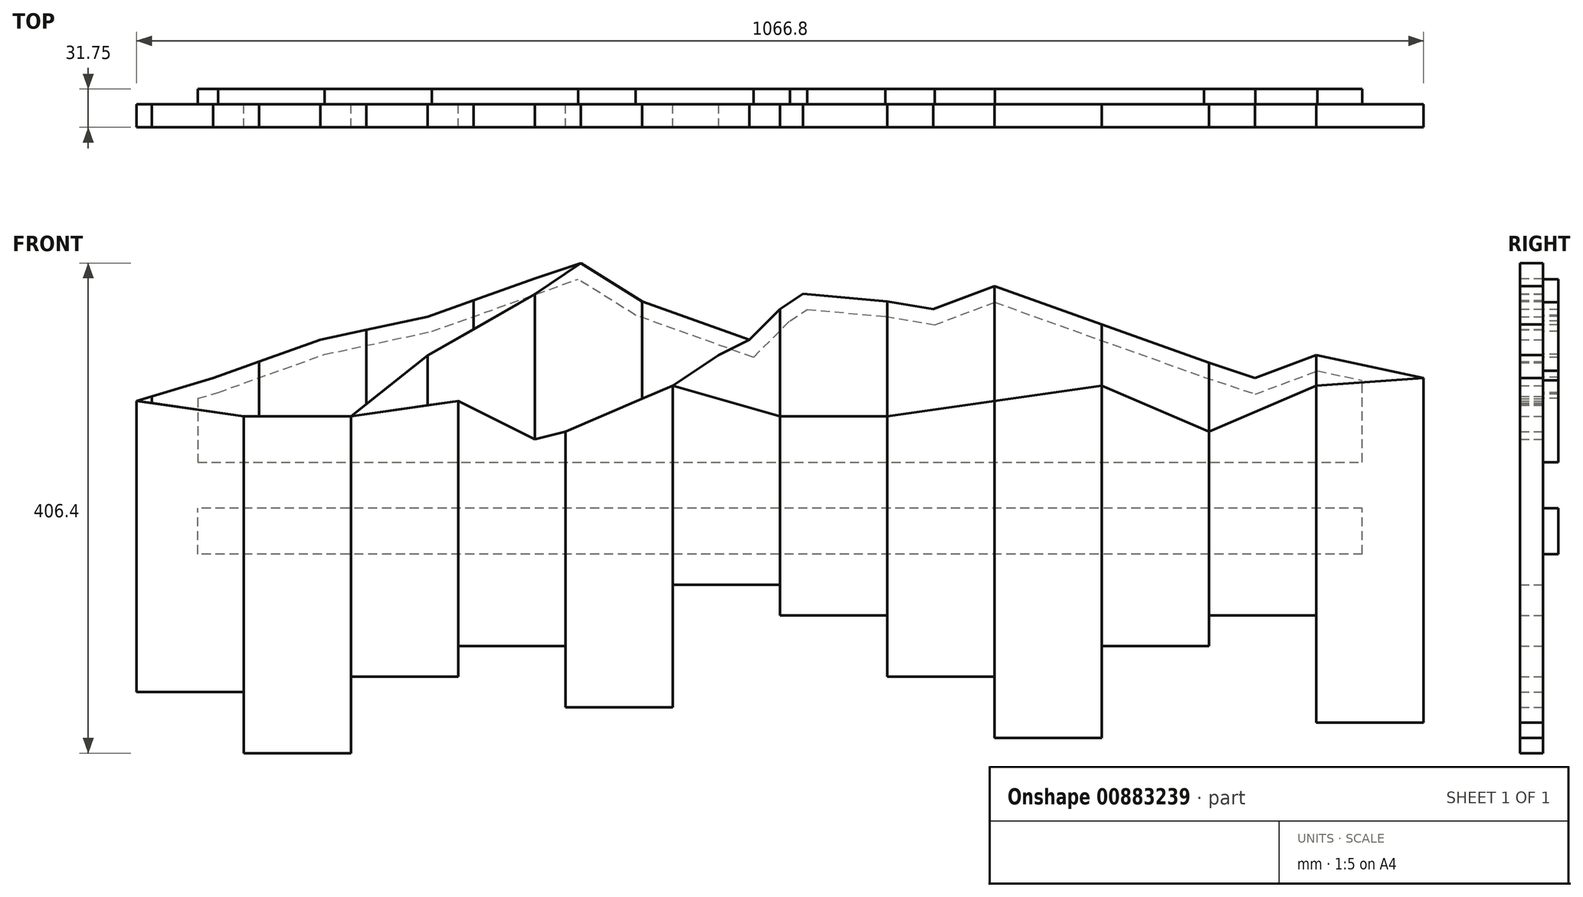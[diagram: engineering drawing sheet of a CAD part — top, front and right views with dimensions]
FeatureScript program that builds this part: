
annotation { "Feature Type Name" : "Feature", "Feature Type Description" : "" }
export const myFeature = defineFeature(function(context is Context, id is Id, definition is map)
    precondition{}
    {
        {
            var Q0;
            Q0=qCreatedBy(makeId("Front.planeOp"),FACE);
            var sketch = newSketch(context, id + "F0", { "sketchPlane" : qUnion([Q0])});
            skLineSegment(sketch, "E0.right", {"start": v(355.6, 304.8) * mm, "end": v(355.6, 76.2) * mm});
            skLineSegment(sketch, "E1.top", {"start": v(355.6, 76.2) * mm, "end": v(444.5, 76.2) * mm});
            skLineSegment(sketch, "E1.right", {"start": v(444.5, 342.9) * mm, "end": v(444.5, 76.2) * mm});
            skLineSegment(sketch, "E2.top", {"start": v(444.5, 177.8) * mm, "end": v(533.4, 177.8) * mm});
            skLineSegment(sketch, "E2.left", {"start": v(444.5, 342.9) * mm, "end": v(444.5, 177.8) * mm});
            skLineSegment(sketch, "E2.right", {"start": v(533.4, 406.4) * mm, "end": v(533.4, 177.8) * mm});
            skLineSegment(sketch, "E3.top", {"start": v(533.4, 152.4) * mm, "end": v(622.3, 152.4) * mm});
            skLineSegment(sketch, "E3.left", {"start": v(533.4, 406.4) * mm, "end": v(533.4, 152.4) * mm});
            skLineSegment(sketch, "E3.right", {"start": v(622.3, 412.75) * mm, "end": v(622.3, 152.4) * mm});
            skLineSegment(sketch, "E4.top", {"start": v(622.3, 101.6) * mm, "end": v(711.2, 101.6) * mm});
            skLineSegment(sketch, "E4.left", {"start": v(622.3, 412.75) * mm, "end": v(622.3, 101.6) * mm});
            skLineSegment(sketch, "E4.right", {"start": v(711.2, 425.45) * mm, "end": v(711.2, 101.6) * mm});
            skLineSegment(sketch, "E5.bottom", {"start": v(711.2, 425.45) * mm, "end": v(800.1, 393.7) * mm});
            skLineSegment(sketch, "E5.top", {"start": v(711.2, 50.8) * mm, "end": v(800.1, 50.8) * mm});
            skLineSegment(sketch, "E5.left", {"start": v(711.2, 425.45) * mm, "end": v(711.2, 50.8) * mm});
            skLineSegment(sketch, "E5.right", {"start": v(800.1, 393.7) * mm, "end": v(800.1, 50.8) * mm});
            skLineSegment(sketch, "E6.bottom", {"start": v(800.1, 393.7) * mm, "end": v(889, 361.95) * mm});
            skLineSegment(sketch, "E6.top", {"start": v(800.1, 127) * mm, "end": v(889, 127) * mm});
            skLineSegment(sketch, "E6.left", {"start": v(800.1, 393.7) * mm, "end": v(800.1, 127) * mm});
            skLineSegment(sketch, "E6.right", {"start": v(889, 361.95) * mm, "end": v(889, 127) * mm});
            skLineSegment(sketch, "E7.top", {"start": v(889, 152.4) * mm, "end": v(977.9, 152.4) * mm});
            skLineSegment(sketch, "E7.left", {"start": v(889, 361.95) * mm, "end": v(889, 152.4) * mm});
            skLineSegment(sketch, "E7.right", {"start": v(977.9, 368.3) * mm, "end": v(977.9, 152.4) * mm});
            skLineSegment(sketch, "E8.bottom", {"start": v(977.9, 368.3) * mm, "end": v(1066.8, 349.25) * mm});
            skLineSegment(sketch, "E8.top", {"start": v(977.9, 63.5) * mm, "end": v(1066.8, 63.5) * mm});
            skLineSegment(sketch, "E8.left", {"start": v(977.9, 368.3) * mm, "end": v(977.9, 63.5) * mm});
            skLineSegment(sketch, "E8.right", {"start": v(1066.8, 349.25) * mm, "end": v(1066.8, 63.5) * mm});
            skLineSegment(sketch, "E9", {"start": v(482.6, 368.3) * mm, "end": v(508, 381) * mm});
            skLineSegment(sketch, "E10", {"start": v(508, 381) * mm, "end": v(533.4, 406.4) * mm});
            skLineSegment(sketch, "E11", {"start": v(533.4, 406.4) * mm, "end": v(552.45, 419.1) * mm});
            skLineSegment(sketch, "E12", {"start": v(552.45, 419.1) * mm, "end": v(622.3, 412.75) * mm});
            skLineSegment(sketch, "E13", {"start": v(622.3, 412.75) * mm, "end": v(660.4, 406.4) * mm});
            skLineSegment(sketch, "E14", {"start": v(660.4, 406.4) * mm, "end": v(711.2, 425.45) * mm});
            skLineSegment(sketch, "E15", {"start": v(889, 361.95) * mm, "end": v(927.1, 349.25) * mm});
            skLineSegment(sketch, "E16", {"start": v(927.1, 349.25) * mm, "end": v(977.9, 368.3) * mm});
            skLineSegment(sketch, "E17", {"start": v(444.5, 342.9) * mm, "end": v(355.6, 304.8) * mm});
            skLineSegment(sketch, "E18", {"start": v(444.5, 342.9) * mm, "end": v(482.6, 368.3) * mm});
            skLineSegment(sketch, "E19", {"start": v(419.1, 412.75) * mm, "end": v(419.1, 332.01) * mm});
            skLineSegment(sketch, "E20", {"start": v(508, 381) * mm, "end": v(419.1, 412.75) * mm});
            skLineSegment(sketch, "E21", {"start": v(419.1, 412.75) * mm, "end": v(368.3, 444.5) * mm});
            skLineSegment(sketch, "E22", {"start": v(368.3, 444.5) * mm, "end": v(330.2, 431.8) * mm});
            skLineSegment(sketch, "E23", {"start": v(330.2, 418.65) * mm, "end": v(330.2, 298.45) * mm});
            skLineSegment(sketch, "E24", {"start": v(355.6, 127) * mm, "end": v(266.7, 127) * mm});
            skLineSegment(sketch, "E25", {"start": v(241.3, 400.05) * mm, "end": v(330.2, 431.8) * mm});
            skLineSegment(sketch, "E26", {"start": v(266.7, 127) * mm, "end": v(266.7, 101.6) * mm});
            skLineSegment(sketch, "E27", {"start": v(266.7, 101.6) * mm, "end": v(177.8, 101.6) * mm});
            skLineSegment(sketch, "E28", {"start": v(152.4, 381) * mm, "end": v(241.3, 400.05) * mm});
            skLineSegment(sketch, "E29", {"start": v(177.8, 101.6) * mm, "end": v(177.8, 38.1) * mm});
            skLineSegment(sketch, "E30", {"start": v(177.8, 38.1) * mm, "end": v(88.9, 38.1) * mm});
            skLineSegment(sketch, "E31", {"start": v(88.9, 38.1) * mm, "end": v(88.9, 88.9) * mm});
            skLineSegment(sketch, "E32", {"start": v(63.5, 349.25) * mm, "end": v(152.4, 381) * mm});
            skLineSegment(sketch, "E33", {"start": v(88.9, 88.9) * mm, "end": v(0, 88.9) * mm});
            skLineSegment(sketch, "E34", {"start": v(0, 88.9) * mm, "end": v(0, 330.2) * mm});
            skLineSegment(sketch, "E35", {"start": v(0, 330.2) * mm, "end": v(63.5, 349.25) * mm});
            skLineSegment(sketch, "E36", {"start": v(355.6, 304.8) * mm, "end": v(330.2, 298.45) * mm});
            skLineSegment(sketch, "E37", {"start": v(330.2, 298.45) * mm, "end": v(266.7, 330.2) * mm});
            skLineSegment(sketch, "E38", {"start": v(266.7, 330.2) * mm, "end": v(177.8, 317.5) * mm});
            skLineSegment(sketch, "E39", {"start": v(177.8, 317.5) * mm, "end": v(88.9, 317.5) * mm});
            skLineSegment(sketch, "E40", {"start": v(88.9, 317.5) * mm, "end": v(0, 330.2) * mm});
            skLineSegment(sketch, "E41", {"start": v(444.5, 342.9) * mm, "end": v(533.4, 317.5) * mm});
            skLineSegment(sketch, "E42", {"start": v(533.4, 317.5) * mm, "end": v(622.3, 317.5) * mm});
            skLineSegment(sketch, "E43", {"start": v(622.3, 317.5) * mm, "end": v(711.2, 330.2) * mm});
            skLineSegment(sketch, "E44", {"start": v(711.2, 330.2) * mm, "end": v(800.1, 342.9) * mm});
            skLineSegment(sketch, "E45", {"start": v(800.1, 342.9) * mm, "end": v(889, 304.8) * mm});
            skLineSegment(sketch, "E46", {"start": v(889, 304.8) * mm, "end": v(977.9, 342.9) * mm});
            skLineSegment(sketch, "E47", {"start": v(977.9, 342.9) * mm, "end": v(1066.8, 349.25) * mm});
            skLineSegment(sketch, "E48", {"start": v(88.9, 88.9) * mm, "end": v(88.9, 317.5) * mm});
            skLineSegment(sketch, "E49", {"start": v(177.8, 317.5) * mm, "end": v(177.8, 101.6) * mm});
            skLineSegment(sketch, "E50", {"start": v(266.7, 127) * mm, "end": v(266.7, 330.2) * mm});
            skLineSegment(sketch, "E51", {"start": v(241.3, 367.85) * mm, "end": v(241.3, 326.57) * mm});
            skLineSegment(sketch, "E52", {"start": v(177.8, 317.5) * mm, "end": v(241.3, 367.85) * mm});
            skLineSegment(sketch, "E53", {"start": v(241.3, 367.85) * mm, "end": v(330.2, 418.65) * mm});
            skLineSegment(sketch, "E54", {"start": v(330.2, 418.65) * mm, "end": v(368.3, 444.5) * mm});
            skLineSegment(sketch, "E55", {"start": v(279.4, 389.62) * mm, "end": v(279.4, 413.66) * mm});
            skLineSegment(sketch, "E56", {"start": v(190.5, 389.16) * mm, "end": v(190.5, 327.57) * mm});
            skLineSegment(sketch, "E57", {"start": v(101.6, 317.5) * mm, "end": v(101.6, 362.86) * mm});
            skLineSegment(sketch, "E58", {"start": v(12.7, 328.39) * mm, "end": v(12.7, 334) * mm});
            skSolve(sketch);
        }
        {
            var Q0;
            {var subQ2=sQuery(id+"F0.wireOp",EDGE,"LQD4jnqJ-VVKP-TUF1-lYmQ-XA3RlbFvOFgd");Q0=makeQuery(id+"F0.imprint","IMPRINT",FACE,{"disambiguationData":[TD([[makeQuery(id+"F0.imprint","IMPRINT",EDGE,{"derivedFrom":subQ2}),1.0]])]});}
            var Q1;
            Q1=makeQuery(id+"F0.imprint","IMPRINT",FACE,{"disambiguationData":[TD([[makeQuery(id+"F0.imprint","IMPRINT",EDGE,{"derivedFrom":sQuery(id+"F0.wireOp",EDGE,"E9")}),1.0]])]});
            var Q2;
            {var subQ0=sQuery(id+"F0.wireOp",EDGE,"E2.top");Q2=makeQuery(id+"F0.imprint","IMPRINT",FACE,{"disambiguationData":[TD([[makeQuery(id+"F0.imprint","IMPRINT",EDGE,{"derivedFrom":subQ0}),1.0]])]});}
            var Q3;
            {var subQ0=sQuery(id+"F0.wireOp",EDGE,"E11");Q3=makeQuery(id+"F0.imprint","IMPRINT",FACE,{"disambiguationData":[TD([[makeQuery(id+"F0.imprint","IMPRINT",EDGE,{"derivedFrom":subQ0}),-1.0]])]});}
            var Q4;
            {var subQ2=sQuery(id+"F0.wireOp",EDGE,"E4.top");Q4=makeQuery(id+"F0.imprint","IMPRINT",FACE,{"disambiguationData":[TD([[makeQuery(id+"F0.imprint","IMPRINT",EDGE,{"derivedFrom":subQ2}),1.0]])]});}
            var Q5;
            {var subQ0=sQuery(id+"F0.wireOp",EDGE,"E5.bottom");Q5=makeQuery(id+"F0.imprint","IMPRINT",FACE,{"disambiguationData":[TD([[makeQuery(id+"F0.imprint","IMPRINT",EDGE,{"derivedFrom":subQ0}),-1.0]])]});}
            var Q6;
            {var subQ4=sQuery(id+"F0.wireOp",EDGE,"E6.top");Q6=makeQuery(id+"F0.imprint","IMPRINT",FACE,{"disambiguationData":[TD([[makeQuery(id+"F0.imprint","IMPRINT",EDGE,{"derivedFrom":subQ4}),1.0]])]});}
            var Q7;
            {var subQ0=sQuery(id+"F0.wireOp",EDGE,"E15");Q7=makeQuery(id+"F0.imprint","IMPRINT",FACE,{"disambiguationData":[TD([[makeQuery(id+"F0.imprint","IMPRINT",EDGE,{"derivedFrom":subQ0}),-1.0]])]});}
            var Q8;
            {var subQ2=sQuery(id+"F0.wireOp",EDGE,"E8.top");Q8=makeQuery(id+"F0.imprint","IMPRINT",FACE,{"disambiguationData":[TD([[makeQuery(id+"F0.imprint","IMPRINT",EDGE,{"derivedFrom":subQ2}),1.0]])]});}
            var Q9;
            {var subQ1=sQuery(id+"F0.wireOp",EDGE,"E24");Q9=makeQuery(id+"F0.imprint","IMPRINT",FACE,{"disambiguationData":[TD([[makeQuery(id+"F0.imprint","IMPRINT",EDGE,{"derivedFrom":subQ1}),-1.0]])]});}
            var Q10;
            Q10=makeQuery(id+"F0.imprint","IMPRINT",FACE,{"disambiguationData":[TD([[makeQuery(id+"F0.imprint","IMPRINT",EDGE,{"derivedFrom":sQuery(id+"F0.wireOp",EDGE,"E33")}),-1.0]])]});
            var Q11;
            {var subQ7=sQuery(id+"F0.wireOp",EDGE,"E56");Q11=makeQuery(id+"F0.imprint","IMPRINT",FACE,{"disambiguationData":[TD([[makeQuery(id+"F0.imprint","IMPRINT",EDGE,{"derivedFrom":subQ7}),-1.0]])]});}
            var Q12;
            {var subQ2=sQuery(id+"F0.wireOp",EDGE,"E22");Q12=makeQuery(id+"F0.imprint","IMPRINT",FACE,{"disambiguationData":[TD([[makeQuery(id+"F0.imprint","IMPRINT",EDGE,{"derivedFrom":subQ2}),1.0]])]});}
            extrude(context, id + "F1", {"entities" : qUnion([Q0, Q1, Q2, Q3, Q4, Q5, Q6, Q7, Q8, Q9, Q10, Q11, Q12]), "depth" : 19.05 * mm, "offsetDistance" : 25.4 * mm});
        }
        {
            var Q0;
            {var subQ0=sQuery(id+"F0.wireOp",EDGE,"E8.bottom");Q0=makeQuery(id+"F0.imprint","IMPRINT",FACE,{"disambiguationData":[TD([[makeQuery(id+"F0.imprint","IMPRINT",EDGE,{"derivedFrom":subQ0}),-1.0]])]});}
            var Q1;
            {var subQ0=sQuery(id+"F0.wireOp",EDGE,"E7.top");Q1=makeQuery(id+"F0.imprint","IMPRINT",FACE,{"disambiguationData":[TD([[makeQuery(id+"F0.imprint","IMPRINT",EDGE,{"derivedFrom":subQ0}),1.0]])]});}
            var Q2;
            {var subQ0=sQuery(id+"F0.wireOp",EDGE,"E6.bottom");Q2=makeQuery(id+"F0.imprint","IMPRINT",FACE,{"disambiguationData":[TD([[makeQuery(id+"F0.imprint","IMPRINT",EDGE,{"derivedFrom":subQ0}),-1.0]])]});}
            var Q3;
            {var subQ3=sQuery(id+"F0.wireOp",EDGE,"E5.top");Q3=makeQuery(id+"F0.imprint","IMPRINT",FACE,{"disambiguationData":[TD([[makeQuery(id+"F0.imprint","IMPRINT",EDGE,{"derivedFrom":subQ3}),1.0]])]});}
            var Q4;
            {var subQ2=sQuery(id+"F0.wireOp",EDGE,"E13");Q4=makeQuery(id+"F0.imprint","IMPRINT",FACE,{"disambiguationData":[TD([[makeQuery(id+"F0.imprint","IMPRINT",EDGE,{"derivedFrom":subQ2}),-1.0]])]});}
            var Q5;
            {var subQ1=sQuery(id+"F0.wireOp",EDGE,"E3.top");Q5=makeQuery(id+"F0.imprint","IMPRINT",FACE,{"disambiguationData":[TD([[makeQuery(id+"F0.imprint","IMPRINT",EDGE,{"derivedFrom":subQ1}),1.0]])]});}
            var Q6;
            Q6=makeQuery(id+"F0.imprint","IMPRINT",FACE,{"disambiguationData":[TD([[makeQuery(id+"F0.imprint","IMPRINT",EDGE,{"derivedFrom":sQuery(id+"F0.wireOp",EDGE,"E9")}),-1.0]])]});
            var Q7;
            {var subQ0=sQuery(id+"F0.wireOp",EDGE,"E1.top");Q7=makeQuery(id+"F0.imprint","IMPRINT",FACE,{"disambiguationData":[TD([[makeQuery(id+"F0.imprint","IMPRINT",EDGE,{"derivedFrom":subQ0}),1.0]])]});}
            var Q8;
            Q8=makeQuery(id+"F0.imprint","IMPRINT",FACE,{"disambiguationData":[TD([[makeQuery(id+"F0.imprint","IMPRINT",EDGE,{"derivedFrom":sQuery(id+"F0.wireOp",EDGE,"E23")}),-1.0]])]});
            var Q9;
            Q9=makeQuery(id+"F0.imprint","IMPRINT",FACE,{"disambiguationData":[TD([[makeQuery(id+"F0.imprint","IMPRINT",EDGE,{"derivedFrom":sQuery(id+"F0.wireOp",EDGE,"E29")}),-1.0]])]});
            var Q10;
            {var subQ0=sQuery(id+"F0.wireOp",EDGE,"E35");Q10=makeQuery(id+"F0.imprint","IMPRINT",FACE,{"disambiguationData":[TD([[makeQuery(id+"F0.imprint","IMPRINT",EDGE,{"derivedFrom":subQ0}),-1.0]])]});}
            var Q11;
            Q11=makeQuery(id+"F1.opExtrude","CAP_FACE",FACE,{"disambiguationData":[OSD([sQuery(id+"F0.wireOp",EDGE,"E2.top"),sQuery(id+"F0.wireOp",EDGE,"E2.left"),sQuery(id+"F0.wireOp",EDGE,"E3.left"),sQuery(id+"F0.wireOp",EDGE,"E41")])],"isStart":false});
            extrude(context, id + "F2", {"entities" : qUnion([Q0, Q1, Q2, Q3, Q4, Q5, Q6, Q7, Q8, Q9, Q10]), "endBound" : BoundingType.UP_TO_SURFACE, "depth" : 25.4 * mm, "endBoundEntityFace" : qUnion([Q11]), "offsetDistance" : 25.4 * mm});
        }
        {
            var Q0;
            {var subQ0=sQuery(id+"F0.wireOp",EDGE,"E19");Q0=makeQuery(id+"F0.imprint","IMPRINT",FACE,{"disambiguationData":[TD([[makeQuery(id+"F0.imprint","IMPRINT",EDGE,{"derivedFrom":subQ0}),-1.0]])]});}
            var Q1;
            {var subQ3=sQuery(id+"F0.wireOp",EDGE,"E51");Q1=makeQuery(id+"F0.imprint","IMPRINT",FACE,{"disambiguationData":[TD([[makeQuery(id+"F0.imprint","IMPRINT",EDGE,{"derivedFrom":subQ3}),-1.0]])]});}
            var Q2;
            {var subQ4=sQuery(id+"F0.wireOp",EDGE,"E57");Q2=makeQuery(id+"F0.imprint","IMPRINT",FACE,{"disambiguationData":[TD([[makeQuery(id+"F0.imprint","IMPRINT",EDGE,{"derivedFrom":subQ4}),1.0]])]});}
            var Q3;
            Q3=makeQuery(id+"F1.opExtrude","CAP_FACE",FACE,{"disambiguationData":[OSD([sQuery(id+"F0.wireOp",EDGE,"E0.right"),sQuery(id+"F0.wireOp",EDGE,"E24"),sQuery(id+"F0.wireOp",EDGE,"E36"),sQuery(id+"F0.wireOp",EDGE,"E37"),sQuery(id+"F0.wireOp",EDGE,"E50")])],"isStart":false});
            extrude(context, id + "F3", {"entities" : qUnion([Q0, Q1, Q2]), "endBound" : BoundingType.UP_TO_SURFACE, "depth" : 25.4 * mm, "endBoundEntityFace" : qUnion([Q3]), "offsetDistance" : 25.4 * mm});
        }
        {
            var Q0;
            {var subQ3=sQuery(id+"F0.wireOp",EDGE,"E55");Q0=makeQuery(id+"F0.imprint","IMPRINT",FACE,{"disambiguationData":[TD([[makeQuery(id+"F0.imprint","IMPRINT",EDGE,{"derivedFrom":subQ3}),1.0]])]});}
            var Q1;
            Q1=makeQuery(id+"F0.imprint","IMPRINT",FACE,{"disambiguationData":[TD([[makeQuery(id+"F0.imprint","IMPRINT",EDGE,{"derivedFrom":sQuery(id+"F0.wireOp",EDGE,"E26")}),-1.0]])]});
            var Q2;
            Q2=makeQuery(id+"F2.opExtrude","CAP_FACE",FACE,{"disambiguationData":[OSD([sQuery(id+"F0.wireOp",EDGE,"E23"),sQuery(id+"F0.wireOp",EDGE,"E37"),sQuery(id+"F0.wireOp",EDGE,"E38"),sQuery(id+"F0.wireOp",EDGE,"E51"),sQuery(id+"F0.wireOp",EDGE,"E53")])],"isStart":false});
            extrude(context, id + "F4", {"entities" : qUnion([Q0, Q1]), "endBound" : BoundingType.UP_TO_SURFACE, "depth" : 25.4 * mm, "endBoundEntityFace" : qUnion([Q2]), "offsetDistance" : 25.4 * mm});
        }
        {
            var Q0;
            Q0=makeQuery(id+"F1.opExtrude","CAP_FACE",FACE,{"disambiguationData":[OSD([sQuery(id+"F0.wireOp",EDGE,"E2.top"),sQuery(id+"F0.wireOp",EDGE,"E2.left"),sQuery(id+"F0.wireOp",EDGE,"E3.left"),sQuery(id+"F0.wireOp",EDGE,"E41")])],"isStart":true});
            var sketch = newSketch(context, id + "F5", { "sketchPlane" : qUnion([Q0])});
            skLineSegment(sketch, "E59.bottom", {"start": v(-1016, 203.2) * mm, "end": v(-50.8, 203.2) * mm});
            skLineSegment(sketch, "E59.top", {"start": v(-1016, 241.3) * mm, "end": v(-50.8, 241.3) * mm});
            skLineSegment(sketch, "E59.left", {"start": v(-1016, 203.2) * mm, "end": v(-1016, 241.3) * mm});
            skLineSegment(sketch, "E59.right", {"start": v(-50.8, 203.2) * mm, "end": v(-50.8, 241.3) * mm});
            skLineSegment(sketch, "E60.0", {"start": v(-978.88, 355.1) * mm, "end": v(-1016, 347.15) * mm});
            skLineSegment(sketch, "E60.1", {"start": v(-927.35, 335.78) * mm, "end": v(-978.88, 355.1) * mm});
            skLineSegment(sketch, "E60.2", {"start": v(-884.86, 349.94) * mm, "end": v(-927.35, 335.78) * mm});
            skLineSegment(sketch, "E60.3", {"start": v(-800.1, 380.21) * mm, "end": v(-884.86, 349.94) * mm});
            skLineSegment(sketch, "E60.4", {"start": v(-711.3, 411.93) * mm, "end": v(-800.1, 380.21) * mm});
            skLineSegment(sketch, "E60.5", {"start": v(-661.67, 393.31) * mm, "end": v(-711.3, 411.93) * mm});
            skLineSegment(sketch, "E60.6", {"start": v(-620.68, 400.14) * mm, "end": v(-661.67, 393.31) * mm});
            skLineSegment(sketch, "E60.7", {"start": v(-244.78, 387.8) * mm, "end": v(-365.86, 431.05) * mm});
            skLineSegment(sketch, "E60.8", {"start": v(-155.88, 368.76) * mm, "end": v(-244.78, 387.8) * mm});
            skLineSegment(sketch, "E60.9", {"start": v(-67.46, 337.18) * mm, "end": v(-155.88, 368.76) * mm});
            skLineSegment(sketch, "E60.10", {"start": v(-50.8, 332.18) * mm, "end": v(-67.46, 337.18) * mm});
            skLineSegment(sketch, "E60.12", {"start": v(-413.53, 401.25) * mm, "end": v(-365.86, 431.05) * mm});
            skLineSegment(sketch, "E60.13", {"start": v(-511.3, 366.34) * mm, "end": v(-413.53, 401.25) * mm});
            skLineSegment(sketch, "E60.14", {"start": v(-511.3, 366.34) * mm, "end": v(-541.5, 396.53) * mm});
            skLineSegment(sketch, "E60.15", {"start": v(-541.5, 396.53) * mm, "end": v(-555.76, 406.05) * mm});
            skLineSegment(sketch, "E60.16", {"start": v(-555.76, 406.05) * mm, "end": v(-620.68, 400.14) * mm});
            skLineSegment(sketch, "E61", {"start": v(-50.8, 332.18) * mm, "end": v(-50.8, 279.4) * mm});
            skLineSegment(sketch, "E62", {"start": v(-50.8, 279.4) * mm, "end": v(-1016, 279.4) * mm});
            skLineSegment(sketch, "E63", {"start": v(-1016, 279.4) * mm, "end": v(-1016, 347.15) * mm});
            skSolve(sketch);
        }
        {
            var Q0;
            Q0 = qSketchRegion(id + "F5", true);
            extrude(context, id + "F6", {"entities" : qUnion([Q0]), "depth" : 12.7 * mm, "offsetDistance" : 25.4 * mm});
        }
    });
